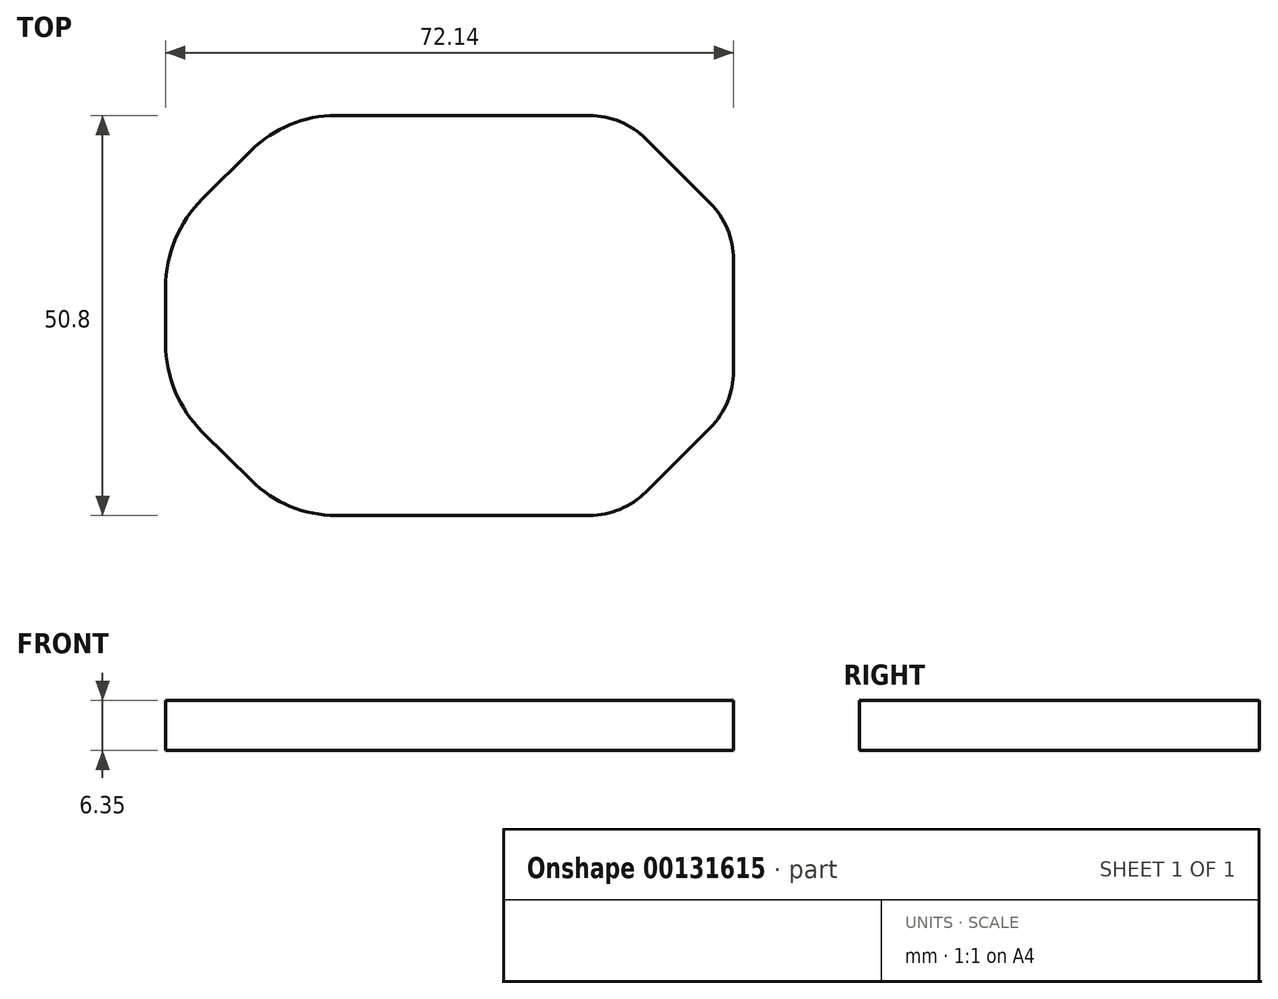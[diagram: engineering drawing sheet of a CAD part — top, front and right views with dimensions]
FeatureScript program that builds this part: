
annotation { "Feature Type Name" : "Feature", "Feature Type Description" : "" }
export const myFeature = defineFeature(function(context is Context, id is Id, definition is map)
    precondition{}
    {
        {
            var Q0;
            Q0=qCreatedBy(makeId("Top.planeOp"),FACE);
            var sketch = newSketch(context, id + "F0", { "sketchPlane" : qUnion([Q0])});
            skLineSegment(sketch, "E0.bottom", {"start": v(0, 20.4) * mm, "end": v(0, 34.59) * mm});
            skLineSegment(sketch, "E0.top", {"start": v(-72.14, 23.9) * mm, "end": v(-72.14, 31.1) * mm});
            skLineSegment(sketch, "E0.left", {"start": v(-18.3, 2.1) * mm, "end": v(-50.5, 2.1) * mm});
            skLineSegment(sketch, "E0.right", {"start": v(-18.3, 52.9) * mm, "end": v(-50.5, 52.9) * mm});
            skLineSegment(sketch, "E1", {"start": v(-11.12, 5.07) * mm, "end": v(-2.98, 13.21) * mm});
            skArc(sketch, "E2.filletArc", {"start": v(-18.3, 2.1) * mm, "mid": v(-14.42, 2.87) * mm, "end": v(-11.12, 5.07) * mm});
            skArc(sketch, "E3.filletArc", {"start": v(-2.98, 13.21) * mm, "mid": v(-0.77, 16.5) * mm, "end": v(0, 20.4) * mm});
            skArc(sketch, "E4.MirrorCS", {"start": v(-18.3, 52.9) * mm, "mid": v(-14.42, 52.12) * mm, "end": v(-11.12, 49.92) * mm});
            skLineSegment(sketch, "E5.MirrorCS", {"start": v(-11.12, 49.92) * mm, "end": v(-2.98, 41.77) * mm});
            skArc(sketch, "E6.MirrorCS", {"start": v(-2.98, 41.77) * mm, "mid": v(-0.77, 38.47) * mm, "end": v(0, 34.59) * mm});
            skLineSegment(sketch, "E7", {"start": v(-61.22, 6.51) * mm, "end": v(-67.48, 12.71) * mm});
            skArc(sketch, "E8.filletArc", {"start": v(-61.22, 6.51) * mm, "mid": v(-56.3, 3.24) * mm, "end": v(-50.5, 2.1) * mm});
            skArc(sketch, "E9.filletArc", {"start": v(-72.14, 23.9) * mm, "mid": v(-70.92, 17.84) * mm, "end": v(-67.48, 12.71) * mm});
            skArc(sketch, "E10.MirrorCS", {"start": v(-61.22, 48.47) * mm, "mid": v(-56.3, 51.74) * mm, "end": v(-50.5, 52.9) * mm});
            skLineSegment(sketch, "E11.MirrorCS", {"start": v(-61.22, 48.47) * mm, "end": v(-67.48, 42.27) * mm});
            skArc(sketch, "E12.MirrorCS", {"start": v(-72.14, 31.1) * mm, "mid": v(-70.92, 37.15) * mm, "end": v(-67.48, 42.27) * mm});
            skSolve(sketch);
        }
        {
            var Q0;
            Q0=qSketchRegion(id+"F0",true);
            extrude(context, id + "F1", {"entities" : qUnion([Q0]), "depth" : 6.35 * mm});
        }
    });
